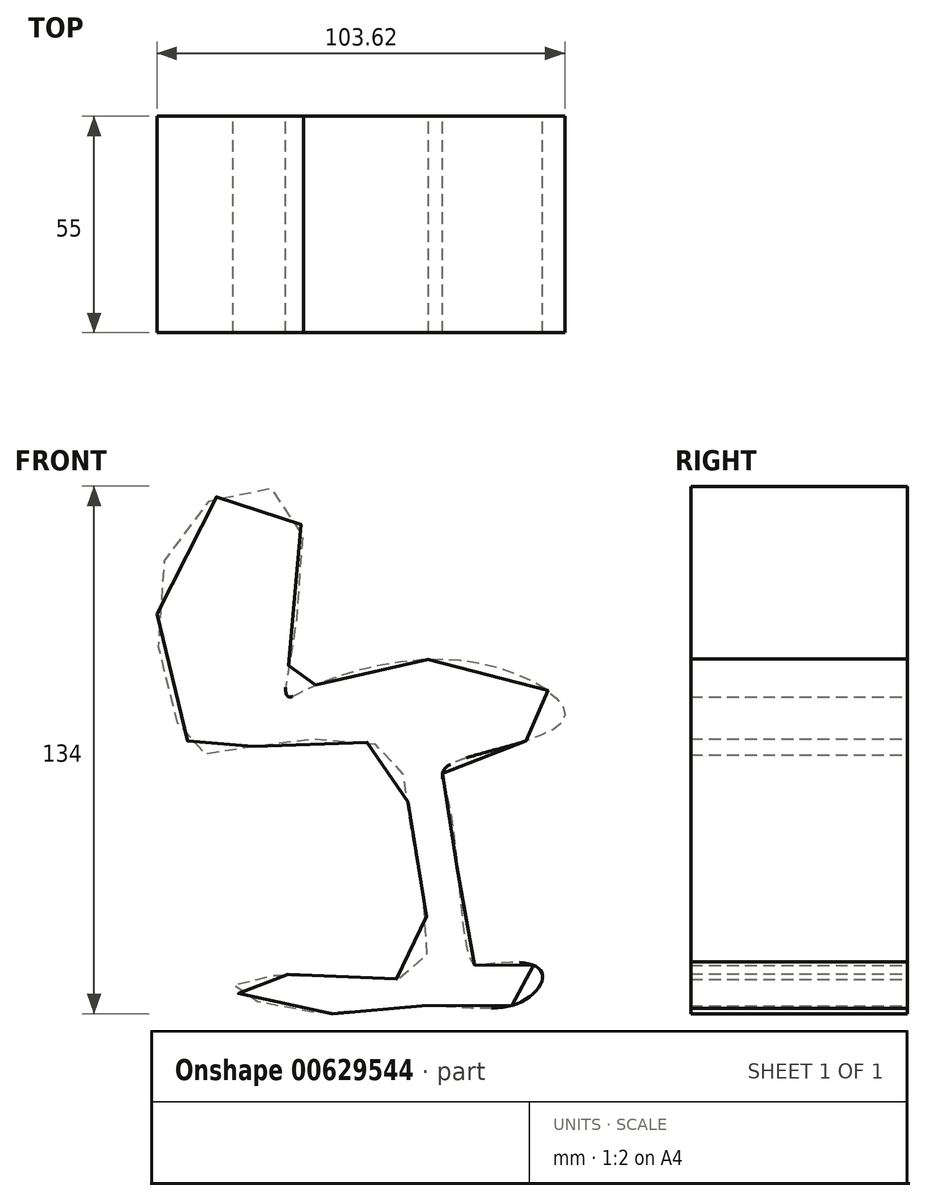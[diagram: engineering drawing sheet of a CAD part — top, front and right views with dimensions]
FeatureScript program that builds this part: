
annotation { "Feature Type Name" : "Feature", "Feature Type Description" : "" }
export const myFeature = defineFeature(function(context is Context, id is Id, definition is map)
    precondition{}
    {
        {
            var Q0;
            Q0=qCreatedBy(makeId("Front.planeOp"),FACE);
            var sketch = newSketch(context, id + "F0", { "sketchPlane" : qUnion([Q0])});
            skFitSpline(sketch, "E0", {"points": [v(-6.76, -72.45) * mm, v(-33.78, -74.32) * mm, v(-54.75, -67.8) * mm, v(-32.38, -64.53) * mm, v(-6.76, -62.67) * mm, v(-9.55, -27.26) * mm, v(-16.07, -7.22) * mm, v(-52.88, -7.22) * mm, v(-65.46, -6.3) * mm, v(-69.2, 47.3) * mm, v(-39.37, 54.75) * mm, v(-41.24, 6.76) * mm, v(-35.64, 8.15) * mm, v(7.69, 14.68) * mm, v(29.12, 0) * mm, v(0, -11.42) * mm, v(0, -20.73) * mm, v(5.82, -61.27) * mm, v(10.48, -61.74) * mm, v(23.53, -63.6) * mm, v(18.4, -71.52) * mm, v(-6.76, -72.45) * mm]});
            skSolve(sketch);
        }
        {
            var Q0;
            Q0 = qSketchRegion(id + "F0", true);
            extrude(context, id + "F1", {"entities" : qUnion([Q0]), "depth" : 55 * mm, "offsetDistance" : 25.4 * mm});
        }
    });
